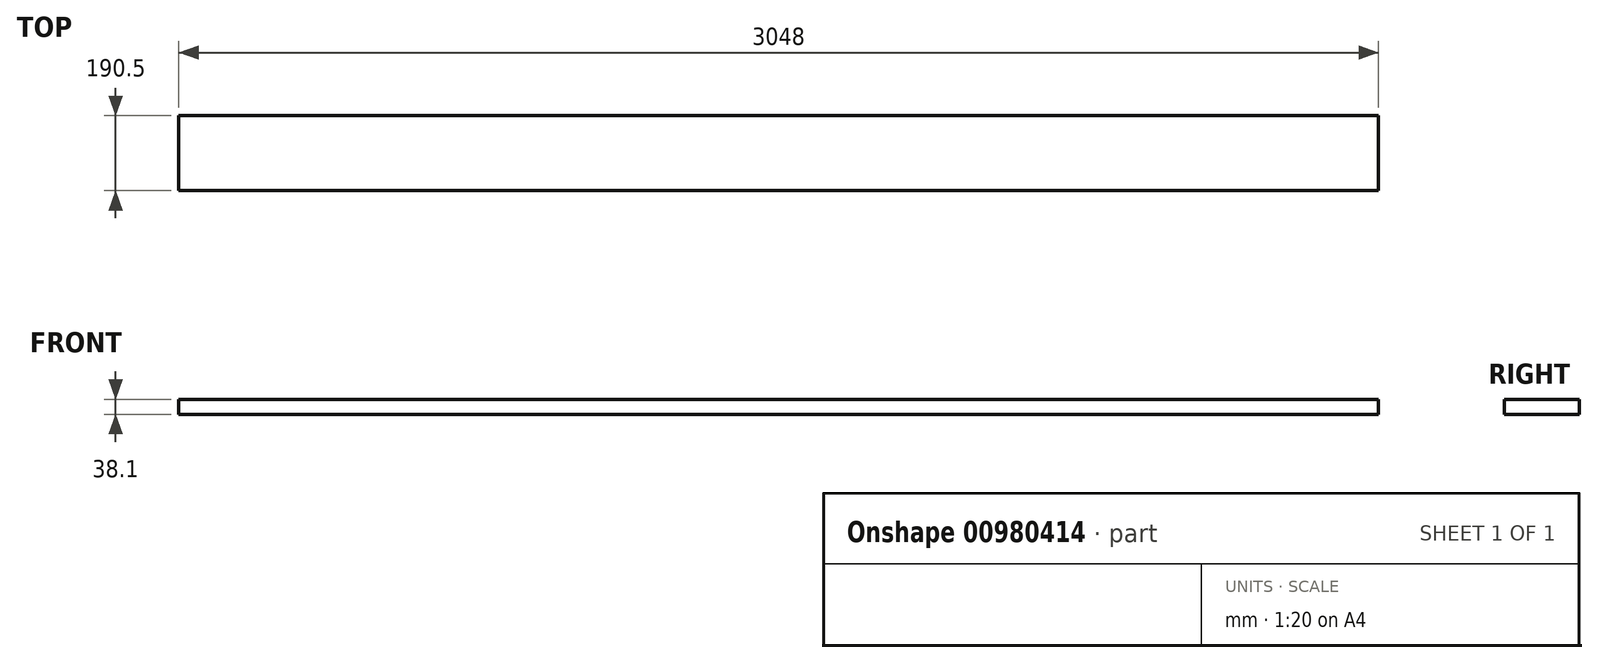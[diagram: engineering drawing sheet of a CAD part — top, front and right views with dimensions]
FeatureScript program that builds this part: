
annotation { "Feature Type Name" : "Feature", "Feature Type Description" : "" }
export const myFeature = defineFeature(function(context is Context, id is Id, definition is map)
    precondition{}
    {
        {
            var Q0;
            Q0=qCreatedBy(makeId("Right.planeOp"),FACE);
            var sketch = newSketch(context, id + "F0", { "sketchPlane" : qUnion([Q0])});
            skLineSegment(sketch, "E0.bottom", {"start": v(95.25, -19.05) * mm, "end": v(-95.25, -19.05) * mm});
            skLineSegment(sketch, "E0.top", {"start": v(95.25, 19.05) * mm, "end": v(-95.25, 19.05) * mm});
            skLineSegment(sketch, "E0.left", {"start": v(95.25, -19.05) * mm, "end": v(95.25, 19.05) * mm});
            skLineSegment(sketch, "E0.right", {"start": v(-95.25, -19.05) * mm, "end": v(-95.25, 19.05) * mm});
            skPoint(sketch, "E0.middle", {"position": v(0, 0) * mm});
            skSolve(sketch);
        }
        {
            var Q0;
            Q0=qSketchRegion(id+"F0",true);
            var Q1;
            Q1=makeQuery(id+"F0.imprint","IMPRINT",FACE,{"disambiguationData":[TD([[makeQuery(id+"F0.imprint","IMPRINT",EDGE,{"derivedFrom":sQuery(id+"F0.wireOp",EDGE,"E0.bottom")}),-1.0]])]});
            extrude(context, id + "F1", {"entities" : qUnion([Q0, Q1]), "depth" : 3048 * mm, "offsetDistance" : 25.4 * mm});
        }
    });
